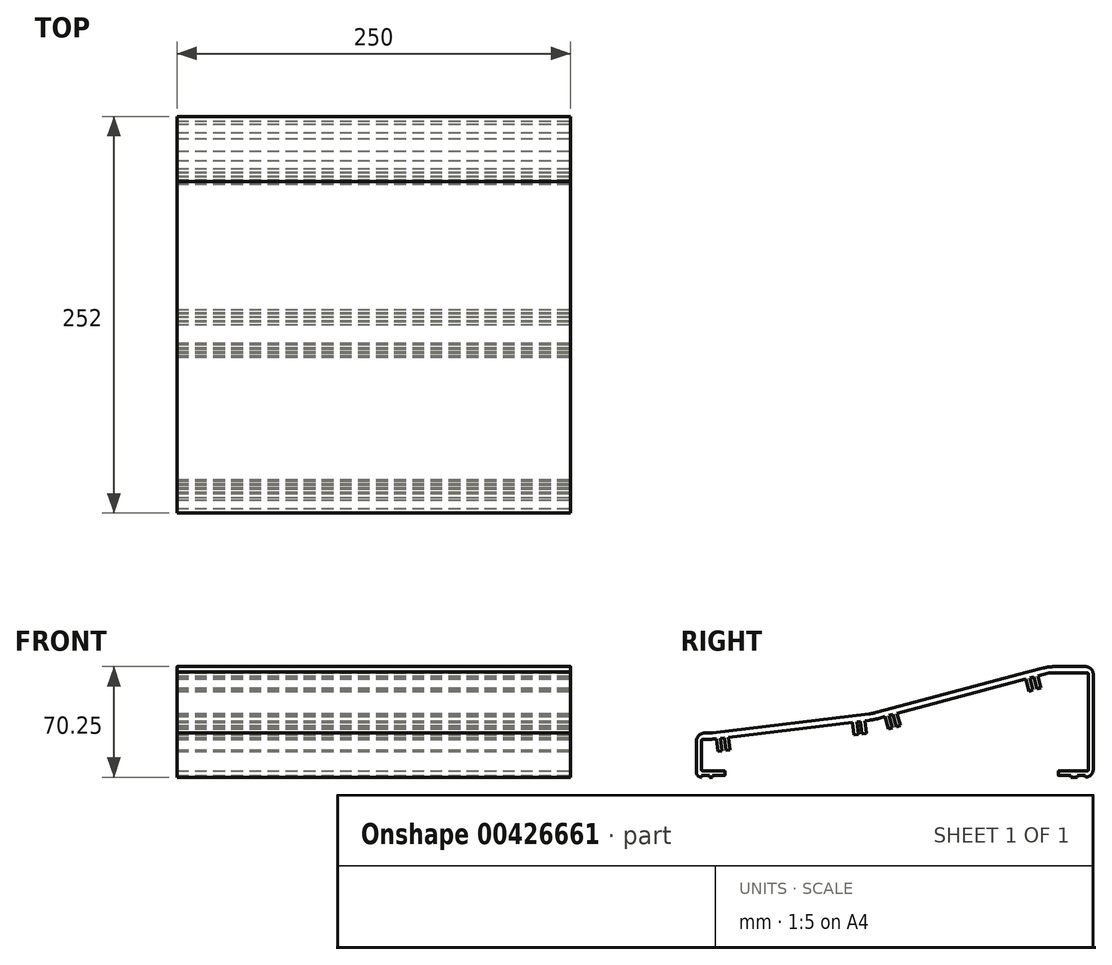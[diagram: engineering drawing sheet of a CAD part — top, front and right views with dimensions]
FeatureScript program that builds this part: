
annotation { "Feature Type Name" : "Feature", "Feature Type Description" : "" }
export const myFeature = defineFeature(function(context is Context, id is Id, definition is map)
    precondition{}
    {
        {
            var Q0;
            Q0=qCreatedBy(makeId("Right.planeOp"),FACE);
            var sketch = newSketch(context, id + "F0", { "sketchPlane" : qUnion([Q0])});
            skLineSegment(sketch, "E0", {"start": v(-67.21, 3) * mm, "end": v(-67.21, 23) * mm});
            skLineSegment(sketch, "E1", {"start": v(-62.21, 28) * mm, "end": v(-60.21, 28) * mm});
            skLineSegment(sketch, "E2", {"start": v(-57.1, 28.19) * mm, "end": v(42.18, 40.15) * mm});
            skLineSegment(sketch, "E3", {"start": v(46.7, 41.02) * mm, "end": v(143.32, 66.82) * mm});
            skPoint(sketch, "E4.visualSharp", {"position": v(-67.21, 28) * mm});
            skArc(sketch, "E4.filletArc", {"start": v(-62.21, 28) * mm, "mid": v(-65.75, 26.54) * mm, "end": v(-67.21, 23) * mm});
            skPoint(sketch, "E5.visualSharp", {"position": v(184.79, 70.25) * mm});
            skPoint(sketch, "E6.visualSharp", {"position": v(150.58, 68.76) * mm});
            skPoint(sketch, "E7.visualSharp", {"position": v(44.47, 40.43) * mm});
            skArc(sketch, "E7.filletArc", {"start": v(42.18, 40.15) * mm, "mid": v(44.46, 40.5) * mm, "end": v(46.7, 41.02) * mm});
            skPoint(sketch, "E8.visualSharp", {"position": v(-58.65, 28) * mm});
            skArc(sketch, "E8.filletArc", {"start": v(-60.21, 28) * mm, "mid": v(-58.65, 28.05) * mm, "end": v(-57.1, 28.19) * mm});
            skLineSegment(sketch, "E9.1", {"start": v(156.59, 66.23) * mm, "end": v(180.79, 66.25) * mm});
            skLineSegment(sketch, "E9.3", {"start": v(47.73, 37.16) * mm, "end": v(156.59, 66.23) * mm});
            skArc(sketch, "E9.4", {"start": v(42.66, 36.18) * mm, "mid": v(45.21, 36.58) * mm, "end": v(47.73, 37.16) * mm});
            skLineSegment(sketch, "E9.6", {"start": v(-63.21, 24) * mm, "end": v(-60.21, 24) * mm});
            skArc(sketch, "E9.7", {"start": v(-60.21, 24) * mm, "mid": v(-58.41, 24.05) * mm, "end": v(-56.62, 24.22) * mm});
            skLineSegment(sketch, "E9.8", {"start": v(-56.62, 24.22) * mm, "end": v(42.66, 36.18) * mm});
            skLineSegment(sketch, "E10", {"start": v(-59.01, 0) * mm, "end": v(-57.2, 0) * mm});
            skPoint(sketch, "E11.visualSharp", {"position": v(-67.21, 0) * mm});
            skArc(sketch, "E11.filletArc", {"start": v(-67.21, 3) * mm, "mid": v(-66.33, 0.88) * mm, "end": v(-64.21, 0) * mm});
            skLineSegment(sketch, "E12", {"start": v(170.59, 0) * mm, "end": v(174.59, 0) * mm});
            skPoint(sketch, "E13.visualSharp", {"position": v(181.57, 0) * mm});
            skLineSegment(sketch, "E14.0", {"start": v(-64.21, 5) * mm, "end": v(-64.21, 23) * mm});
            skLineSegment(sketch, "E15", {"start": v(160.42, 70.23) * mm, "end": v(179.78, 70.25) * mm});
            skLineSegment(sketch, "E16", {"start": v(184.79, 65.25) * mm, "end": v(184.79, 5) * mm});
            skArc(sketch, "E17.filletArc", {"start": v(184.79, 65.25) * mm, "mid": v(183.32, 68.78) * mm, "end": v(179.78, 70.25) * mm});
            skLineSegment(sketch, "E18", {"start": v(181.79, 5) * mm, "end": v(181.79, 65.25) * mm});
            skPoint(sketch, "E19.visualSharp", {"position": v(181.79, 66.25) * mm});
            skArc(sketch, "E19.filletArc", {"start": v(181.79, 65.25) * mm, "mid": v(181.5, 65.95) * mm, "end": v(180.79, 66.25) * mm});
            skArc(sketch, "E20.filletArc", {"start": v(-63.21, 24) * mm, "mid": v(-63.92, 23.7) * mm, "end": v(-64.21, 23) * mm});
            skLineSegment(sketch, "E21", {"start": v(-64.21, 0) * mm, "end": v(-64.21, 1) * mm});
            skLineSegment(sketch, "E22", {"start": v(-64.21, 1) * mm, "end": v(-59.01, 1) * mm});
            skLineSegment(sketch, "E23", {"start": v(-59.01, 1) * mm, "end": v(-59.01, 0) * mm});
            skLineSegment(sketch, "E24", {"start": v(179.79, 0) * mm, "end": v(179.79, 1) * mm});
            skLineSegment(sketch, "E25", {"start": v(179.79, 1) * mm, "end": v(174.59, 1) * mm});
            skLineSegment(sketch, "E26", {"start": v(174.59, 1) * mm, "end": v(174.59, 0) * mm});
            skPoint(sketch, "E27.visualSharp", {"position": v(184.79, 0) * mm});
            skArc(sketch, "E27.filletArc", {"start": v(179.79, 0) * mm, "mid": v(183.32, 1.46) * mm, "end": v(184.79, 5) * mm});
            skLineSegment(sketch, "E28", {"start": v(-57.2, 0) * mm, "end": v(-57.2, 1) * mm});
            skLineSegment(sketch, "E29", {"start": v(-57.2, 1) * mm, "end": v(-49.4, 1) * mm});
            skLineSegment(sketch, "E30", {"start": v(-49.2, 1.2) * mm, "end": v(-49.2, 3.8) * mm});
            skLineSegment(sketch, "E31", {"start": v(-49.4, 4) * mm, "end": v(-63.21, 4) * mm});
            skArc(sketch, "E32.filletArc", {"start": v(-64.21, 5) * mm, "mid": v(-63.92, 4.3) * mm, "end": v(-63.21, 4) * mm});
            skPoint(sketch, "E33.visualSharp", {"position": v(-49.2, 4) * mm});
            skArc(sketch, "E33.filletArc", {"start": v(-49.2, 3.8) * mm, "mid": v(-49.25, 3.94) * mm, "end": v(-49.4, 4) * mm});
            skPoint(sketch, "E34.visualSharp", {"position": v(-49.2, 1) * mm});
            skArc(sketch, "E34.filletArc", {"start": v(-49.4, 1) * mm, "mid": v(-49.25, 1.06) * mm, "end": v(-49.2, 1.2) * mm});
            skLineSegment(sketch, "E35", {"start": v(170.59, 0) * mm, "end": v(170.59, 1) * mm});
            skLineSegment(sketch, "E36", {"start": v(170.59, 1) * mm, "end": v(162.79, 1) * mm});
            skLineSegment(sketch, "E37", {"start": v(162.59, 1.2) * mm, "end": v(162.59, 3.8) * mm});
            skLineSegment(sketch, "E38", {"start": v(162.79, 4) * mm, "end": v(180.79, 4) * mm});
            skArc(sketch, "E39.filletArc", {"start": v(180.79, 4) * mm, "mid": v(181.5, 4.3) * mm, "end": v(181.79, 5) * mm});
            skPoint(sketch, "E40.visualSharp", {"position": v(162.59, 4) * mm});
            skArc(sketch, "E40.filletArc", {"start": v(162.79, 4) * mm, "mid": v(162.65, 3.94) * mm, "end": v(162.59, 3.8) * mm});
            skPoint(sketch, "E41.visualSharp", {"position": v(162.59, 1) * mm});
            skArc(sketch, "E41.filletArc", {"start": v(162.59, 1.2) * mm, "mid": v(162.65, 1.06) * mm, "end": v(162.79, 1) * mm});
            skPoint(sketch, "E42.orphan", {"position": v(-50.17, 0) * mm});
            skLineSegment(sketch, "E43", {"start": v(-54.62, 24.46) * mm, "end": v(-53.66, 16.51) * mm});
            skLineSegment(sketch, "E44", {"start": v(-53.66, 16.51) * mm, "end": v(-50.98, 16.84) * mm});
            skLineSegment(sketch, "E45", {"start": v(-50.98, 16.84) * mm, "end": v(-51.94, 24.78) * mm});
            skLineSegment(sketch, "E46", {"start": v(-49.46, 25.08) * mm, "end": v(-48.5, 17.14) * mm});
            skLineSegment(sketch, "E47", {"start": v(-48.5, 17.14) * mm, "end": v(-45.82, 17.46) * mm});
            skLineSegment(sketch, "E48", {"start": v(-45.82, 17.46) * mm, "end": v(-46.78, 25.4) * mm});
            skLineSegment(sketch, "E49", {"start": v(153.03, 69.3) * mm, "end": v(143.32, 66.82) * mm});
            skPoint(sketch, "E50.visualSharp", {"position": v(156.66, 70.23) * mm});
            skArc(sketch, "E50.filletArc", {"start": v(160.42, 70.23) * mm, "mid": v(156.7, 70) * mm, "end": v(153.03, 69.3) * mm});
            skLineSegment(sketch, "E51", {"start": v(31.87, 34.88) * mm, "end": v(32.83, 26.94) * mm});
            skLineSegment(sketch, "E52", {"start": v(32.83, 26.94) * mm, "end": v(35.5, 27.26) * mm});
            skLineSegment(sketch, "E53", {"start": v(35.5, 27.26) * mm, "end": v(34.55, 35.2) * mm});
            skLineSegment(sketch, "E54", {"start": v(37.03, 35.5) * mm, "end": v(37.99, 27.56) * mm});
            skLineSegment(sketch, "E55", {"start": v(37.99, 27.56) * mm, "end": v(40.67, 27.88) * mm});
            skLineSegment(sketch, "E56", {"start": v(40.67, 27.88) * mm, "end": v(39.71, 35.83) * mm});
            skLineSegment(sketch, "E57", {"start": v(52.53, 38.44) * mm, "end": v(54.6, 30.71) * mm});
            skLineSegment(sketch, "E58", {"start": v(54.6, 30.71) * mm, "end": v(57.2, 31.4) * mm});
            skLineSegment(sketch, "E59", {"start": v(57.2, 31.4) * mm, "end": v(55.14, 39.14) * mm});
            skLineSegment(sketch, "E60", {"start": v(57.56, 39.78) * mm, "end": v(59.62, 32.05) * mm});
            skLineSegment(sketch, "E61", {"start": v(59.62, 32.05) * mm, "end": v(62.23, 32.75) * mm});
            skLineSegment(sketch, "E62", {"start": v(62.23, 32.75) * mm, "end": v(60.16, 40.48) * mm});
            skLineSegment(sketch, "E63", {"start": v(149.55, 64.35) * mm, "end": v(151.61, 56.62) * mm});
            skLineSegment(sketch, "E64", {"start": v(151.61, 56.62) * mm, "end": v(149, 55.92) * mm});
            skLineSegment(sketch, "E65", {"start": v(149, 55.92) * mm, "end": v(146.94, 63.65) * mm});
            skLineSegment(sketch, "E66", {"start": v(144.53, 63) * mm, "end": v(146.59, 55.28) * mm});
            skLineSegment(sketch, "E67", {"start": v(146.59, 55.28) * mm, "end": v(143.98, 54.58) * mm});
            skLineSegment(sketch, "E68", {"start": v(143.98, 54.58) * mm, "end": v(141.92, 62.3) * mm});
            skSolve(sketch);
        }
        {
            var Q0;
            Q0 = qSketchRegion(id + "F0", true);
            extrude(context, id + "F1", {"entities" : qUnion([Q0]), "oppositeDirection" : true, "depth" : 250 * mm});
        }
    });
